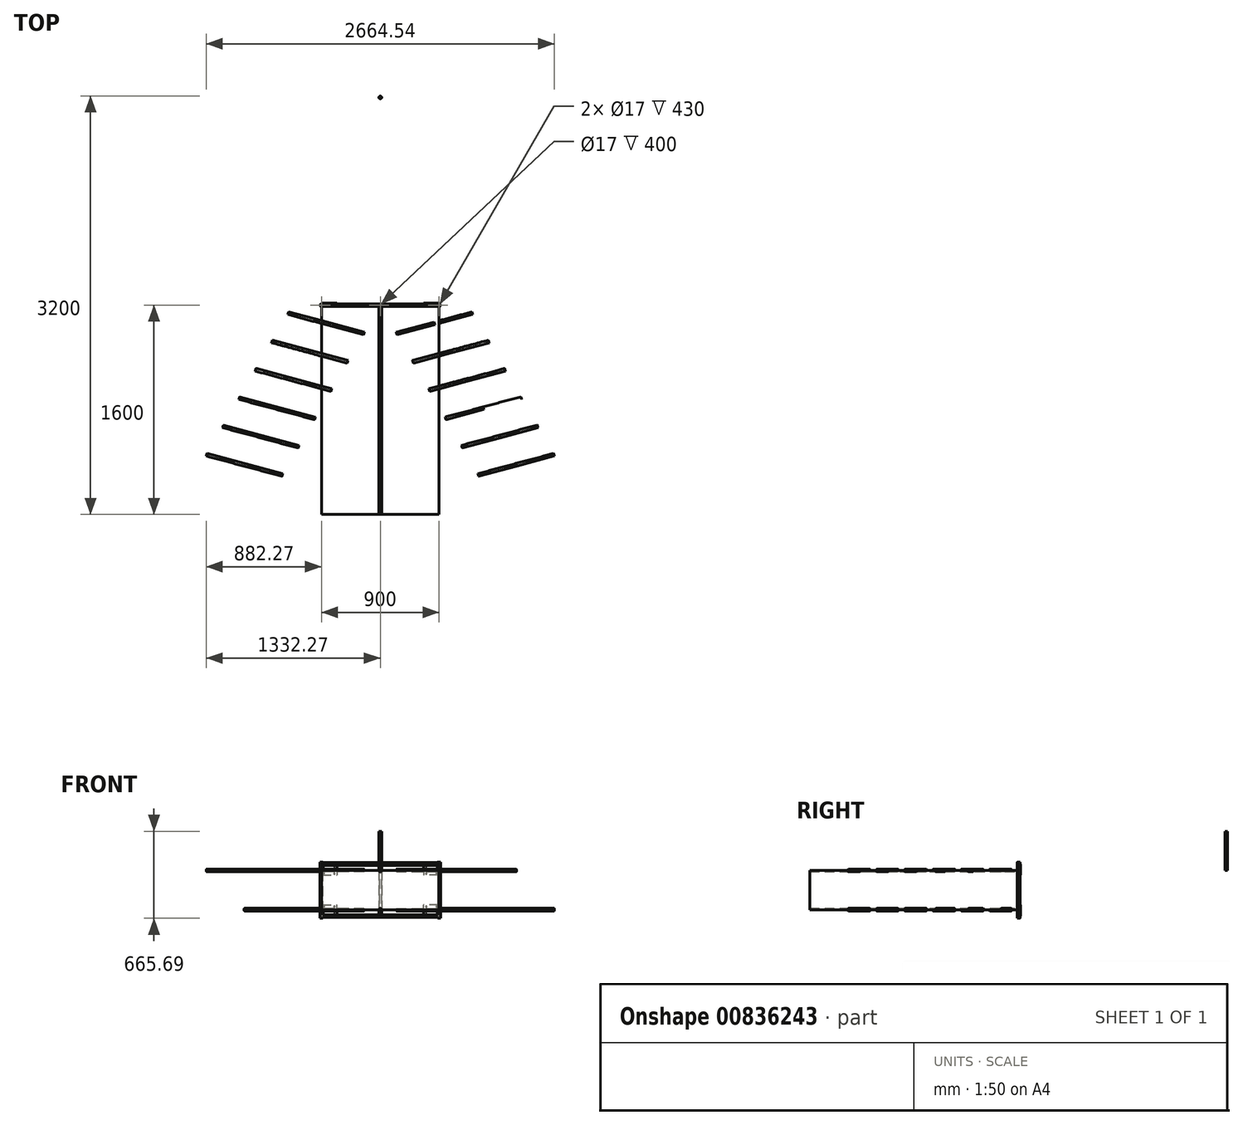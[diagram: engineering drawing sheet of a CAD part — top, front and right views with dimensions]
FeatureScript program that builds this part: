
annotation { "Feature Type Name" : "Feature", "Feature Type Description" : "" }
export const myFeature = defineFeature(function(context is Context, id is Id, definition is map)
    precondition{}
    {
        {
            var Q0;
            Q0=qCreatedBy(makeId("Front.planeOp"),FACE);
            var sketch = newSketch(context, id + "F0", { "sketchPlane" : qUnion([Q0])});
            skLineSegment(sketch, "E0.bottom", {"start": v(450, -150) * mm, "end": v(10.5, -150) * mm});
            skLineSegment(sketch, "E0.left", {"start": v(450, -150) * mm, "end": v(450, 150) * mm});
            skLineSegment(sketch, "E0.right", {"start": v(-450, -150) * mm, "end": v(-450, 150) * mm});
            skPoint(sketch, "E0.middle", {"position": v(0, 0) * mm});
            skLineSegment(sketch, "E1.trimOffspring", {"start": v(-15, 150) * mm, "end": v(-450, 150) * mm});
            skLineSegment(sketch, "E2.trimOffspring", {"start": v(-15, -150) * mm, "end": v(-450, -150) * mm});
            skLineSegment(sketch, "E3", {"start": v(450, -150) * mm, "end": v(-450, -150) * mm});
            skLineSegment(sketch, "E4", {"start": v(-450, 150) * mm, "end": v(450, 150) * mm});
            skCircle(sketch, "E5", {"center": v(0, 150) * mm, "radius": 10.5 * mm});
            skCircle(sketch, "E6", {"center": v(0, -150) * mm, "radius": 10.5 * mm});
            skSolve(sketch);
        }
        {
            var Q0;
            Q0=sQuery(id+"F0.wireOp",EDGE,"E4");
            cPoint(context, id + "F1", {"entities" : qUnion([Q0]), "parameter" : 0.5});
        }
        {
            var Q0;
            Q0=sQuery(id+"F0.wireOp",EDGE,"E4");
            var Q1;
            Q1 = qCreatedBy(id + "F1" ,VERTEX);
            cPlane(context, id + "F2", {"entities" : qUnion([Q0, Q1]), "cplaneType" : CPlaneType.LINE_POINT, "offset" : 25 * mm, "width" : 150 * mm, "height" : 150 * mm});
        }
        {
            var Q0;
            Q0=sQuery(id+"F0.wireOp",EDGE,"E3");
            cPoint(context, id + "F3", {"entities" : qUnion([Q0]), "parameter" : 0.5});
        }
        {
            var Q0;
            Q0 = qCreatedBy(id + "F3" ,VERTEX);
            var Q1;
            Q1=sQuery(id+"F0.wireOp",EDGE,"E3");
            cPlane(context, id + "F4", {"entities" : qUnion([Q0, Q1]), "cplaneType" : CPlaneType.LINE_POINT, "offset" : 25 * mm, "width" : 150 * mm, "height" : 150 * mm});
        }
        {
            var Q0;
            Q0=sQuery(id+"F0.wireOp",EDGE,"E0.left");
            cPoint(context, id + "F5", {"entities" : qUnion([Q0]), "parameter" : 0.5});
        }
        {
            var Q0;
            Q0=sQuery(id+"F0.wireOp",EDGE,"E0.left");
            var Q1;
            Q1 = qCreatedBy(id + "F5" ,VERTEX);
            cPlane(context, id + "F6", {"entities" : qUnion([Q0, Q1]), "cplaneType" : CPlaneType.LINE_POINT, "offset" : 25 * mm, "width" : 150 * mm, "height" : 150 * mm});
        }
        {
            var Q0;
            {var subQ0=sQuery(id+"F0.wireOp",EDGE,"E6");var subQ1=sQuery(id+"F0.wireOp",EDGE,"E3");var subQ2=makeQuery(id+"F0.imprint","INTERSECT",VERTEX,{"disambiguationData":[OD(0.0)],"derivedFrom":[subQ1,subQ0]});Q0=makeQuery(id+"F0.imprint","IMPRINT",FACE,{"disambiguationData":[TD([[makeQuery(id+"F0.imprint","IMPRINT",EDGE,{"disambiguationData":[TD([[subQ2,-1.0]])],"derivedFrom":subQ1}),1.0]])]});}
            var Q1;
            {var subQ0=sQuery(id+"F0.wireOp",EDGE,"E5");var subQ1=sQuery(id+"F0.wireOp",EDGE,"E4");var subQ2=makeQuery(id+"F0.imprint","INTERSECT",VERTEX,{"disambiguationData":[OD(0.0)],"derivedFrom":[subQ1,subQ0]});Q1=makeQuery(id+"F0.imprint","IMPRINT",FACE,{"disambiguationData":[TD([[makeQuery(id+"F0.imprint","IMPRINT",EDGE,{"disambiguationData":[TD([[subQ2,-1.0]])],"derivedFrom":subQ1}),1.0]])]});}
            var Q2;
            {var subQ0=sQuery(id+"F0.wireOp",EDGE,"E6");var subQ1=sQuery(id+"F0.wireOp",EDGE,"E3");var subQ2=makeQuery(id+"F0.imprint","INTERSECT",VERTEX,{"disambiguationData":[OD(0.0)],"derivedFrom":[subQ1,subQ0]});Q2=makeQuery(id+"F0.imprint","IMPRINT",FACE,{"disambiguationData":[TD([[makeQuery(id+"F0.imprint","IMPRINT",EDGE,{"disambiguationData":[TD([[subQ2,-1.0]])],"derivedFrom":subQ1}),-1.0]])]});}
            var Q3;
            {var subQ0=sQuery(id+"F0.wireOp",EDGE,"E5");var subQ1=sQuery(id+"F0.wireOp",EDGE,"E4");var subQ2=makeQuery(id+"F0.imprint","INTERSECT",VERTEX,{"disambiguationData":[OD(0.0)],"derivedFrom":[subQ1,subQ0]});Q3=makeQuery(id+"F0.imprint","IMPRINT",FACE,{"disambiguationData":[TD([[makeQuery(id+"F0.imprint","IMPRINT",EDGE,{"disambiguationData":[TD([[subQ2,-1.0]])],"derivedFrom":subQ1}),-1.0]])]});}
            extrude(context, id + "F7", {"entities" : qUnion([Q0, Q1, Q2, Q3]), "depth" : 1600 * mm, "offsetDistance" : 25 * mm});
        }
        {
            var Q0;
            Q0=qCreatedBy(id+"F4.planeOp",FACE);
            var sketch = newSketch(context, id + "F8", { "sketchPlane" : qUnion([Q0])});
            skCircle(sketch, "E7", {"center": v(0, -198.47) * mm, "radius": 10.5 * mm});
            skSolve(sketch);
        }
        {
            var Q0;
            Q0 = qSketchRegion(id + "F8", true);
            extrude(context, id + "F9", {"entities" : qUnion([Q0]), "operationType" : NewBodyOperationType.ADD, "depth" : 450 * mm, "offsetDistance" : 25 * mm, "hasSecondDirection" : true, "secondDirectionOppositeDirection" : true, "secondDirectionDepth" : 450 * mm});
        }
        {
            var Q0;
            Q0=qCreatedBy(id+"F2.planeOp",FACE);
            var sketch = newSketch(context, id + "F10", { "sketchPlane" : qUnion([Q0])});
            skCircle(sketch, "E8", {"center": v(0, 199.3) * mm, "radius": 10.5 * mm});
            skSolve(sketch);
        }
        {
            var Q0;
            Q0 = qSketchRegion(id + "F10", true);
            extrude(context, id + "F11", {"entities" : qUnion([Q0]), "operationType" : NewBodyOperationType.ADD, "depth" : 450 * mm, "offsetDistance" : 25 * mm, "hasSecondDirection" : true, "secondDirectionOppositeDirection" : true, "secondDirectionDepth" : 450 * mm});
        }
        {
            var Q0;
            Q0=qCreatedBy(id+"F6.planeOp",FACE);
            var sketch = newSketch(context, id + "F12", { "sketchPlane" : qUnion([Q0])});
            skCircle(sketch, "E9", {"center": v(450, 0) * mm, "radius": 10.5 * mm});
            skSolve(sketch);
        }
        {
            var Q0;
            Q0=makeQuery(id+"F11.opExtrude","CAP_FACE",FACE,{"disambiguationData":[OSD([sQuery(id+"F10.wireOp",EDGE,"E8")])],"isStart":true});
            var sketch = newSketch(context, id + "F13", { "sketchPlane" : qUnion([Q0])});
            skLineSegment(sketch, "E10", {"start": v(0, 199.3) * mm, "end": v(0, -200.7) * mm});
            skSolve(sketch);
        }
        {
            var Q0;
            Q0=sQuery(id+"F13.wireOp",EDGE,"E10");
            cPoint(context, id + "F14", {"entities" : qUnion([Q0]), "parameter" : 0.5});
        }
        {
            var Q0;
            Q0=sQuery(id+"F13.wireOp",EDGE,"E10");
            var Q1;
            Q1 = qCreatedBy(id + "F14" ,VERTEX);
            cPlane(context, id + "F15", {"entities" : qUnion([Q0, Q1]), "cplaneType" : CPlaneType.LINE_POINT, "offset" : 25 * mm, "width" : 150 * mm, "height" : 150 * mm});
        }
        {
            var Q0;
            Q0=qCreatedBy(id+"F15.planeOp",FACE);
            var sketch = newSketch(context, id + "F16", { "sketchPlane" : qUnion([Q0])});
            skCircle(sketch, "E11", {"center": v(-450, 0) * mm, "radius": 10.5 * mm});
            skSolve(sketch);
        }
        {
            var Q0;
            Q0=makeQuery(id+"F13.imprint","IMPRINT",FACE,{"disambiguationData":[TD([[makeQuery(id+"F13.imprint","IMPRINT",EDGE,{"derivedFrom":makeQuery(id+"F11.opExtrude","CAP_EDGE",EDGE,{"disambiguationData":[OSD([sQuery(id+"F10.wireOp",EDGE,"E8")])],"isStart":true})}),-1.0]])]});
            var sketch = newSketch(context, id + "F17", { "sketchPlane" : qUnion([Q0])});
            skCircle(sketch, "E12", {"center": v(0, 199.3) * mm, "radius": 8.5 * mm});
            skSolve(sketch);
        }
        {
            var Q0;
            Q0 = qSketchRegion(id + "F17", true);
            extrude(context, id + "F18", {"entities" : qUnion([Q0]), "operationType" : NewBodyOperationType.REMOVE, "oppositeDirection" : true, "depth" : 900 * mm, "offsetDistance" : 25 * mm});
        }
        {
            var Q0;
            Q0=makeQuery(id+"F9.opExtrude","CAP_FACE",FACE,{"disambiguationData":[OSD([sQuery(id+"F8.wireOp",EDGE,"E7")])],"isStart":false});
            var sketch = newSketch(context, id + "F19", { "sketchPlane" : qUnion([Q0])});
            skCircle(sketch, "E13", {"center": v(0, -198.47) * mm, "radius": 8.5 * mm});
            skSolve(sketch);
        }
        {
            var Q0;
            Q0 = qSketchRegion(id + "F19", true);
            extrude(context, id + "F20", {"entities" : qUnion([Q0]), "operationType" : NewBodyOperationType.REMOVE, "oppositeDirection" : true, "depth" : 900 * mm, "offsetDistance" : 25 * mm});
        }
        {
            var Q0;
            Q0 = qSketchRegion(id + "F12", true);
            extrude(context, id + "F21", {"entities" : qUnion([Q0]), "depth" : 215 * mm, "offsetDistance" : 25 * mm, "hasSecondDirection" : true, "secondDirectionOppositeDirection" : true, "secondDirectionDepth" : 215 * mm});
        }
        {
            var Q0;
            Q0=makeQuery(id+"F21.opExtrude","CAP_FACE",FACE,{"disambiguationData":[OSD([sQuery(id+"F12.wireOp",EDGE,"E9")])],"isStart":false});
            var sketch = newSketch(context, id + "F22", { "sketchPlane" : qUnion([Q0])});
            skCircle(sketch, "E14", {"center": v(450, 0) * mm, "radius": 8.5 * mm});
            skSolve(sketch);
        }
        {
            var Q0;
            Q0 = qSketchRegion(id + "F22", true);
            extrude(context, id + "F23", {"entities" : qUnion([Q0]), "operationType" : NewBodyOperationType.REMOVE, "oppositeDirection" : true, "depth" : 460 * mm, "offsetDistance" : 25 * mm});
        }
        {
            var Q0;
            Q0 = qSketchRegion(id + "F16", true);
            extrude(context, id + "F24", {"entities" : qUnion([Q0]), "depth" : 215 * mm, "offsetDistance" : 25 * mm, "hasSecondDirection" : true, "secondDirectionOppositeDirection" : true, "secondDirectionDepth" : 215 * mm});
        }
        {
            var Q0;
            Q0=makeQuery(id+"F24.opExtrude","CAP_FACE",FACE,{"disambiguationData":[OSD([sQuery(id+"F16.wireOp",EDGE,"E11")])],"isStart":true});
            var sketch = newSketch(context, id + "F25", { "sketchPlane" : qUnion([Q0])});
            skCircle(sketch, "E15", {"center": v(-450, 0) * mm, "radius": 8.5 * mm});
            skSolve(sketch);
        }
        {
            var Q0;
            Q0 = qSketchRegion(id + "F25", true);
            extrude(context, id + "F26", {"entities" : qUnion([Q0]), "operationType" : NewBodyOperationType.REMOVE, "oppositeDirection" : true, "depth" : 460 * mm, "offsetDistance" : 25 * mm});
        }
        {
            var Q0;
            Q0=makeQuery(id+"F7.opExtrude","CAP_FACE",FACE,{"disambiguationData":[OSD([sQuery(id+"F0.wireOp",EDGE,"E5")])],"isStart":false});
            var sketch = newSketch(context, id + "F27", { "sketchPlane" : qUnion([Q0])});
            skCircle(sketch, "E16", {"center": v(0, 150) * mm, "radius": 8.5 * mm});
            skSolve(sketch);
        }
        {
            var Q0;
            Q0 = qSketchRegion(id + "F27", true);
            extrude(context, id + "F28", {"entities" : qUnion([Q0]), "operationType" : NewBodyOperationType.REMOVE, "oppositeDirection" : true, "depth" : 1600 * mm, "offsetDistance" : 25 * mm});
        }
        {
            var Q0;
            Q0=makeQuery(id+"F7.opExtrude","SWEPT_FACE",FACE,{"disambiguationData":[OSD([sQuery(id+"F0.wireOp",EDGE,"E6")])]});
            var Q1;
            Q1=makeQuery(id+"F9.opExtrude","SWEPT_FACE",FACE,{"disambiguationData":[OSD([sQuery(id+"F8.wireOp",EDGE,"E7")])]});
            cPlane(context, id + "F29", {"entities" : qUnion([Q0, Q1]), "cplaneType" : CPlaneType.LINE_ANGLE, "offset" : 25 * mm, "angle" : 0 * degree, "width" : 150 * mm, "height" : 150 * mm});
        }
        {
            var Q0;
            Q0=qCreatedBy(id+"F29.planeOp",FACE);
            var sketch = newSketch(context, id + "F30", { "sketchPlane" : qUnion([Q0])});
            skLineSegment(sketch, "E17", {"start": v(0, 0) * mm, "end": v(0, 1600) * mm});
            skLineSegment(sketch, "E18", {"start": v(0, 250) * mm, "end": v(579.56, 405.3) * mm});
            skLineSegment(sketch, "E19", {"start": v(0, 250) * mm, "end": v(-289.78, 327.65) * mm});
            skLineSegment(sketch, "E20", {"start": v(0, 500) * mm, "end": v(579.56, 655.3) * mm});
            skLineSegment(sketch, "E21", {"start": v(0, 500) * mm, "end": v(-289.78, 577.65) * mm});
            skLineSegment(sketch, "E22", {"start": v(0, 750) * mm, "end": v(579.56, 905.3) * mm});
            skLineSegment(sketch, "E23", {"start": v(0, 750) * mm, "end": v(-289.78, 827.65) * mm});
            skLineSegment(sketch, "E24", {"start": v(0, 1000) * mm, "end": v(579.56, 1155.3) * mm});
            skLineSegment(sketch, "E25", {"start": v(0, 1000) * mm, "end": v(-289.78, 1077.65) * mm});
            skLineSegment(sketch, "E26", {"start": v(0, 1250) * mm, "end": v(579.56, 1405.3) * mm});
            skLineSegment(sketch, "E27", {"start": v(0, 1250) * mm, "end": v(-289.78, 1327.65) * mm});
            skLineSegment(sketch, "E28", {"start": v(0, 1500) * mm, "end": v(579.56, 1655.3) * mm});
            skLineSegment(sketch, "E29", {"start": v(0, 1500) * mm, "end": v(-289.78, 1577.65) * mm});
            skSolve(sketch);
        }
        {
            var Q0;
            Q0=makeQuery(id+"F7.opExtrude","SWEPT_FACE",FACE,{"disambiguationData":[OSD([sQuery(id+"F0.wireOp",EDGE,"E5")])]});
            var Q1;
            Q1=makeQuery(id+"F11.opExtrude","SWEPT_FACE",FACE,{"disambiguationData":[OSD([sQuery(id+"F10.wireOp",EDGE,"E8")])]});
            cPlane(context, id + "F31", {"entities" : qUnion([Q0, Q1]), "cplaneType" : CPlaneType.LINE_ANGLE, "offset" : 25 * mm, "angle" : 0 * degree, "width" : 150 * mm, "height" : 150 * mm});
        }
        {
            var Q0;
            Q0=qCreatedBy(id+"F31.planeOp",FACE);
            var sketch = newSketch(context, id + "F32", { "sketchPlane" : qUnion([Q0])});
            skLineSegment(sketch, "E30", {"start": v(0, 0) * mm, "end": v(0, -1600) * mm});
            skLineSegment(sketch, "E31", {"start": v(0, -250) * mm, "end": v(-579.56, -405.3) * mm});
            skLineSegment(sketch, "E32", {"start": v(0, -500) * mm, "end": v(-579.56, -655.3) * mm});
            skLineSegment(sketch, "E33", {"start": v(0, -750) * mm, "end": v(-579.56, -905.3) * mm});
            skLineSegment(sketch, "E34", {"start": v(0, -1000) * mm, "end": v(-579.56, -1155.3) * mm});
            skLineSegment(sketch, "E35", {"start": v(0, -1250) * mm, "end": v(-579.56, -1405.3) * mm});
            skLineSegment(sketch, "E36", {"start": v(0, -1500) * mm, "end": v(-579.56, -1655.3) * mm});
            skLineSegment(sketch, "E37", {"start": v(0, -250) * mm, "end": v(289.78, -327.65) * mm});
            skLineSegment(sketch, "E38", {"start": v(0, -500) * mm, "end": v(289.78, -577.65) * mm});
            skLineSegment(sketch, "E39", {"start": v(0, -750) * mm, "end": v(289.78, -827.65) * mm});
            skLineSegment(sketch, "E40", {"start": v(0, -1000) * mm, "end": v(289.78, -1077.65) * mm});
            skLineSegment(sketch, "E41", {"start": v(0, -1250) * mm, "end": v(289.78, -1327.65) * mm});
            skLineSegment(sketch, "E42", {"start": v(0, -1500) * mm, "end": v(289.78, -1577.65) * mm});
            skSolve(sketch);
        }
        {
            var Q0;
            Q0=sQuery(id+"F32.wireOp",VERTEX,"E36.start");
            var Q1;
            Q1=sQuery(id+"F32.wireOp",VERTEX,"E36.end");
            cPlane(context, id + "F33", {"entities" : qUnion([Q0, Q1]), "cplaneType" : CPlaneType.MID_PLANE, "offset" : 25 * mm, "oppositeDirection" : true, "width" : 150 * mm, "height" : 150 * mm});
        }
        {
            var Q0;
            Q0=qCreatedBy(id+"F33.planeOp",FACE);
            var sketch = newSketch(context, id + "F34", { "sketchPlane" : qUnion([Q0])});
            skCircle(sketch, "E43", {"center": v(1448.89, 150) * mm, "radius": 10.5 * mm});
            skSolve(sketch);
        }
        {
            var Q0;
            Q0 = qSketchRegion(id + "F34", true);
            extrude(context, id + "F35", {"entities" : qUnion([Q0]), "operationType" : NewBodyOperationType.ADD, "oppositeDirection" : true, "depth" : 300 * mm, "offsetDistance" : 25 * mm, "hasSecondDirection" : true, "secondDirectionOppositeDirection" : false, "secondDirectionDepth" : 300 * mm});
        }
        {
            var Q0;
            Q0=sQuery(id+"F32.wireOp",EDGE,"E35");
            cPlane(context, id + "F36", {"entities" : qUnion([Q0]), "cplaneType" : CPlaneType.MID_PLANE, "offset" : 25 * mm, "width" : 150 * mm, "height" : 150 * mm});
        }
        {
            var Q0;
            Q0=qCreatedBy(id+"F36.planeOp",FACE);
            var sketch = newSketch(context, id + "F37", { "sketchPlane" : qUnion([Q0])});
            skCircle(sketch, "E44", {"center": v(1207.4, 150) * mm, "radius": 10.5 * mm});
            skSolve(sketch);
        }
        {
            var Q0;
            Q0 = qSketchRegion(id + "F37", true);
            extrude(context, id + "F38", {"entities" : qUnion([Q0]), "operationType" : NewBodyOperationType.ADD, "depth" : 300 * mm, "offsetDistance" : 25 * mm, "hasSecondDirection" : true, "secondDirectionOppositeDirection" : true, "secondDirectionDepth" : 300 * mm});
        }
        {
            var Q0;
            Q0=sQuery(id+"F32.wireOp",EDGE,"E34");
            cPlane(context, id + "F39", {"entities" : qUnion([Q0]), "cplaneType" : CPlaneType.MID_PLANE, "offset" : 25 * mm, "width" : 150 * mm, "height" : 150 * mm});
        }
        {
            var Q0;
            Q0=qCreatedBy(id+"F39.planeOp",FACE);
            var sketch = newSketch(context, id + "F40", { "sketchPlane" : qUnion([Q0])});
            skCircle(sketch, "E45", {"center": v(965.93, 150) * mm, "radius": 10.5 * mm});
            skSolve(sketch);
        }
        {
            var Q0;
            Q0 = qSketchRegion(id + "F40", true);
            extrude(context, id + "F41", {"entities" : qUnion([Q0]), "operationType" : NewBodyOperationType.ADD, "depth" : 300 * mm, "offsetDistance" : 25 * mm, "hasSecondDirection" : true, "secondDirectionOppositeDirection" : true, "secondDirectionDepth" : 300 * mm});
        }
        {
            var Q0;
            Q0=sQuery(id+"F32.wireOp",EDGE,"E33");
            cPlane(context, id + "F42", {"entities" : qUnion([Q0]), "cplaneType" : CPlaneType.MID_PLANE, "offset" : 25 * mm, "width" : 150 * mm, "height" : 150 * mm});
        }
        {
            var Q0;
            Q0=qCreatedBy(id+"F42.planeOp",FACE);
            var sketch = newSketch(context, id + "F43", { "sketchPlane" : qUnion([Q0])});
            skCircle(sketch, "E46", {"center": v(724.44, 150) * mm, "radius": 10.5 * mm});
            skSolve(sketch);
        }
        {
            var Q0;
            Q0 = qSketchRegion(id + "F43", true);
            extrude(context, id + "F44", {"entities" : qUnion([Q0]), "operationType" : NewBodyOperationType.ADD, "depth" : 300 * mm, "offsetDistance" : 25 * mm, "hasSecondDirection" : true, "secondDirectionOppositeDirection" : true, "secondDirectionDepth" : 300 * mm});
        }
        {
            var Q0;
            Q0=sQuery(id+"F32.wireOp",EDGE,"E32");
            cPlane(context, id + "F45", {"entities" : qUnion([Q0]), "cplaneType" : CPlaneType.MID_PLANE, "offset" : 25 * mm, "width" : 150 * mm, "height" : 150 * mm});
        }
        {
            var Q0;
            Q0=qCreatedBy(id+"F45.planeOp",FACE);
            var sketch = newSketch(context, id + "F46", { "sketchPlane" : qUnion([Q0])});
            skCircle(sketch, "E47", {"center": v(482.96, 150) * mm, "radius": 10.5 * mm});
            skSolve(sketch);
        }
        {
            var Q0;
            Q0 = qSketchRegion(id + "F46", true);
            extrude(context, id + "F47", {"entities" : qUnion([Q0]), "operationType" : NewBodyOperationType.ADD, "depth" : 300 * mm, "offsetDistance" : 25 * mm, "hasSecondDirection" : true, "secondDirectionOppositeDirection" : true, "secondDirectionDepth" : 300 * mm});
        }
        {
            var Q0;
            Q0=sQuery(id+"F32.wireOp",EDGE,"E31");
            cPlane(context, id + "F48", {"entities" : qUnion([Q0]), "cplaneType" : CPlaneType.MID_PLANE, "offset" : 25 * mm, "width" : 150 * mm, "height" : 150 * mm});
        }
        {
            var Q0;
            Q0=qCreatedBy(id+"F48.planeOp",FACE);
            var sketch = newSketch(context, id + "F49", { "sketchPlane" : qUnion([Q0])});
            skCircle(sketch, "E48", {"center": v(241.48, 150) * mm, "radius": 10.5 * mm});
            skSolve(sketch);
        }
        {
            var Q0;
            Q0 = qSketchRegion(id + "F49", true);
            extrude(context, id + "F50", {"entities" : qUnion([Q0]), "operationType" : NewBodyOperationType.ADD, "depth" : 300 * mm, "offsetDistance" : 25 * mm, "hasSecondDirection" : true, "secondDirectionOppositeDirection" : true, "secondDirectionDepth" : 300 * mm});
        }
        {
            var Q0;
            Q0=sQuery(id+"F30.wireOp",EDGE,"E29");
            cPlane(context, id + "F51", {"entities" : qUnion([Q0]), "cplaneType" : CPlaneType.MID_PLANE, "offset" : 25 * mm, "width" : 150 * mm, "height" : 150 * mm});
        }
        {
            var Q0;
            Q0=qCreatedBy(id+"F51.planeOp",FACE);
            var sketch = newSketch(context, id + "F52", { "sketchPlane" : qUnion([Q0])});
            skCircle(sketch, "E49", {"center": v(1448.89, -150) * mm, "radius": 10.5 * mm});
            skSolve(sketch);
        }
        {
            var Q0;
            Q0 = qSketchRegion(id + "F52", true);
            extrude(context, id + "F53", {"entities" : qUnion([Q0]), "operationType" : NewBodyOperationType.ADD, "depth" : 150 * mm, "offsetDistance" : 25 * mm, "hasSecondDirection" : true, "secondDirectionOppositeDirection" : true, "secondDirectionDepth" : 150 * mm});
        }
        {
            var Q0;
            Q0=sQuery(id+"F30.wireOp",EDGE,"E27");
            cPlane(context, id + "F54", {"entities" : qUnion([Q0]), "cplaneType" : CPlaneType.MID_PLANE, "offset" : 25 * mm, "width" : 150 * mm, "height" : 150 * mm});
        }
        {
            var Q0;
            Q0=qCreatedBy(id+"F54.planeOp",FACE);
            var sketch = newSketch(context, id + "F55", { "sketchPlane" : qUnion([Q0])});
            skCircle(sketch, "E50", {"center": v(1207.4, -150) * mm, "radius": 10.5 * mm});
            skSolve(sketch);
        }
        {
            var Q0;
            Q0 = qSketchRegion(id + "F55", true);
            extrude(context, id + "F56", {"entities" : qUnion([Q0]), "operationType" : NewBodyOperationType.ADD, "depth" : 150 * mm, "offsetDistance" : 25 * mm, "hasSecondDirection" : true, "secondDirectionOppositeDirection" : true, "secondDirectionDepth" : 150 * mm});
        }
        {
            var Q0;
            Q0=sQuery(id+"F30.wireOp",EDGE,"E25");
            cPlane(context, id + "F57", {"entities" : qUnion([Q0]), "cplaneType" : CPlaneType.MID_PLANE, "offset" : 25 * mm, "width" : 150 * mm, "height" : 150 * mm});
        }
        {
            var Q0;
            Q0=qCreatedBy(id+"F57.planeOp",FACE);
            var sketch = newSketch(context, id + "F58", { "sketchPlane" : qUnion([Q0])});
            skCircle(sketch, "E51", {"center": v(965.93, -150) * mm, "radius": 10.5 * mm});
            skSolve(sketch);
        }
        {
            var Q0;
            Q0 = qSketchRegion(id + "F58", true);
            extrude(context, id + "F59", {"entities" : qUnion([Q0]), "operationType" : NewBodyOperationType.ADD, "depth" : 150 * mm, "offsetDistance" : 25 * mm, "hasSecondDirection" : true, "secondDirectionOppositeDirection" : true, "secondDirectionDepth" : 150 * mm});
        }
        {
            var Q0;
            Q0=sQuery(id+"F30.wireOp",EDGE,"E23");
            cPlane(context, id + "F60", {"entities" : qUnion([Q0]), "cplaneType" : CPlaneType.MID_PLANE, "offset" : 25 * mm, "width" : 150 * mm, "height" : 150 * mm});
        }
        {
            var Q0;
            Q0=qCreatedBy(id+"F60.planeOp",FACE);
            var sketch = newSketch(context, id + "F61", { "sketchPlane" : qUnion([Q0])});
            skCircle(sketch, "E52", {"center": v(724.44, -150) * mm, "radius": 10.5 * mm});
            skSolve(sketch);
        }
        {
            var Q0;
            Q0 = qSketchRegion(id + "F61", true);
            extrude(context, id + "F62", {"entities" : qUnion([Q0]), "operationType" : NewBodyOperationType.ADD, "depth" : 150 * mm, "offsetDistance" : 25 * mm, "hasSecondDirection" : true, "secondDirectionOppositeDirection" : true, "secondDirectionDepth" : 150 * mm});
        }
        {
            var Q0;
            Q0=sQuery(id+"F30.wireOp",EDGE,"E21");
            cPlane(context, id + "F63", {"entities" : qUnion([Q0]), "cplaneType" : CPlaneType.MID_PLANE, "offset" : 25 * mm, "width" : 150 * mm, "height" : 150 * mm});
        }
        {
            var Q0;
            Q0=qCreatedBy(id+"F63.planeOp",FACE);
            var sketch = newSketch(context, id + "F64", { "sketchPlane" : qUnion([Q0])});
            skCircle(sketch, "E53", {"center": v(482.96, -150) * mm, "radius": 10.5 * mm});
            skSolve(sketch);
        }
        {
            var Q0;
            Q0 = qSketchRegion(id + "F64", true);
            extrude(context, id + "F65", {"entities" : qUnion([Q0]), "operationType" : NewBodyOperationType.ADD, "depth" : 150 * mm, "offsetDistance" : 25 * mm, "hasSecondDirection" : true, "secondDirectionOppositeDirection" : true, "secondDirectionDepth" : 150 * mm});
        }
        {
            var Q0;
            Q0=sQuery(id+"F30.wireOp",EDGE,"E19");
            cPlane(context, id + "F66", {"entities" : qUnion([Q0]), "cplaneType" : CPlaneType.MID_PLANE, "offset" : 25 * mm, "width" : 150 * mm, "height" : 150 * mm});
        }
        {
            var Q0;
            Q0=qCreatedBy(id+"F66.planeOp",FACE);
            var sketch = newSketch(context, id + "F67", { "sketchPlane" : qUnion([Q0])});
            skCircle(sketch, "E54", {"center": v(241.48, -150) * mm, "radius": 10.5 * mm});
            skSolve(sketch);
        }
        {
            var Q0;
            Q0 = qSketchRegion(id + "F67", true);
            extrude(context, id + "F68", {"entities" : qUnion([Q0]), "operationType" : NewBodyOperationType.ADD, "depth" : 150 * mm, "offsetDistance" : 25 * mm, "hasSecondDirection" : true, "secondDirectionOppositeDirection" : true, "secondDirectionDepth" : 150 * mm});
        }
        {
            var Q0;
            Q0=sQuery(id+"F30.wireOp",EDGE,"E28");
            cPlane(context, id + "F69", {"entities" : qUnion([Q0]), "cplaneType" : CPlaneType.MID_PLANE, "offset" : 25 * mm, "width" : 150 * mm, "height" : 150 * mm});
        }
        {
            var Q0;
            Q0=qCreatedBy(id+"F69.planeOp",FACE);
            var sketch = newSketch(context, id + "F70", { "sketchPlane" : qUnion([Q0])});
            skCircle(sketch, "E55", {"center": v(-1448.89, -150) * mm, "radius": 10.5 * mm});
            skSolve(sketch);
        }
        {
            var Q0;
            Q0 = qSketchRegion(id + "F70", true);
            extrude(context, id + "F71", {"entities" : qUnion([Q0]), "operationType" : NewBodyOperationType.ADD, "depth" : 300 * mm, "offsetDistance" : 25 * mm, "hasSecondDirection" : true, "secondDirectionOppositeDirection" : true, "secondDirectionDepth" : 300 * mm});
        }
        {
            var Q0;
            Q0=sQuery(id+"F30.wireOp",EDGE,"E26");
            cPlane(context, id + "F72", {"entities" : qUnion([Q0]), "cplaneType" : CPlaneType.MID_PLANE, "offset" : 25 * mm, "width" : 150 * mm, "height" : 150 * mm});
        }
        {
            var Q0;
            Q0=qCreatedBy(id+"F72.planeOp",FACE);
            var sketch = newSketch(context, id + "F73", { "sketchPlane" : qUnion([Q0])});
            skCircle(sketch, "E56", {"center": v(-1207.4, -150) * mm, "radius": 10.5 * mm});
            skSolve(sketch);
        }
        {
            var Q0;
            Q0 = qSketchRegion(id + "F73", true);
            extrude(context, id + "F74", {"entities" : qUnion([Q0]), "operationType" : NewBodyOperationType.ADD, "depth" : 300 * mm, "offsetDistance" : 25 * mm, "hasSecondDirection" : true, "secondDirectionOppositeDirection" : true, "secondDirectionDepth" : 300 * mm});
        }
        {
            var Q0;
            Q0=sQuery(id+"F30.wireOp",EDGE,"E24");
            cPlane(context, id + "F75", {"entities" : qUnion([Q0]), "cplaneType" : CPlaneType.MID_PLANE, "offset" : 25 * mm, "width" : 150 * mm, "height" : 150 * mm});
        }
        {
            var Q0;
            Q0=qCreatedBy(id+"F75.planeOp",FACE);
            var sketch = newSketch(context, id + "F76", { "sketchPlane" : qUnion([Q0])});
            skCircle(sketch, "E57", {"center": v(-965.93, -150) * mm, "radius": 10.5 * mm});
            skSolve(sketch);
        }
        {
            var Q0;
            Q0 = qSketchRegion(id + "F76", true);
            extrude(context, id + "F77", {"entities" : qUnion([Q0]), "operationType" : NewBodyOperationType.ADD, "depth" : 300 * mm, "offsetDistance" : 25 * mm, "hasSecondDirection" : true, "secondDirectionOppositeDirection" : true, "secondDirectionDepth" : 300 * mm});
        }
        {
            var Q0;
            Q0=sQuery(id+"F30.wireOp",EDGE,"E22");
            cPlane(context, id + "F78", {"entities" : qUnion([Q0]), "cplaneType" : CPlaneType.MID_PLANE, "offset" : 25 * mm, "width" : 150 * mm, "height" : 150 * mm});
        }
        {
            var Q0;
            Q0=qCreatedBy(id+"F78.planeOp",FACE);
            var sketch = newSketch(context, id + "F79", { "sketchPlane" : qUnion([Q0])});
            skCircle(sketch, "E58", {"center": v(-724.44, -150) * mm, "radius": 10.5 * mm});
            skSolve(sketch);
        }
        {
            var Q0;
            Q0 = qSketchRegion(id + "F79", true);
            extrude(context, id + "F80", {"entities" : qUnion([Q0]), "operationType" : NewBodyOperationType.ADD, "depth" : 300 * mm, "offsetDistance" : 25 * mm, "hasSecondDirection" : true, "secondDirectionOppositeDirection" : true, "secondDirectionDepth" : 300 * mm});
        }
        {
            var Q0;
            Q0=sQuery(id+"F30.wireOp",EDGE,"E20");
            cPlane(context, id + "F81", {"entities" : qUnion([Q0]), "cplaneType" : CPlaneType.MID_PLANE, "offset" : 25 * mm, "width" : 150 * mm, "height" : 150 * mm});
        }
        {
            var Q0;
            Q0=qCreatedBy(id+"F81.planeOp",FACE);
            var sketch = newSketch(context, id + "F82", { "sketchPlane" : qUnion([Q0])});
            skCircle(sketch, "E59", {"center": v(-482.96, -150) * mm, "radius": 10.5 * mm});
            skSolve(sketch);
        }
        {
            var Q0;
            Q0 = qSketchRegion(id + "F82", true);
            extrude(context, id + "F83", {"entities" : qUnion([Q0]), "operationType" : NewBodyOperationType.ADD, "depth" : 300 * mm, "offsetDistance" : 25 * mm, "hasSecondDirection" : true, "secondDirectionOppositeDirection" : true, "secondDirectionDepth" : 300 * mm});
        }
        {
            var Q0;
            Q0=sQuery(id+"F30.wireOp",EDGE,"E18");
            cPlane(context, id + "F84", {"entities" : qUnion([Q0]), "cplaneType" : CPlaneType.MID_PLANE, "offset" : 25 * mm, "width" : 150 * mm, "height" : 150 * mm});
        }
        {
            var Q0;
            Q0=qCreatedBy(id+"F84.planeOp",FACE);
            var sketch = newSketch(context, id + "F85", { "sketchPlane" : qUnion([Q0])});
            skCircle(sketch, "E60", {"center": v(-241.48, -150) * mm, "radius": 10.5 * mm});
            skSolve(sketch);
        }
        {
            var Q0;
            Q0 = qSketchRegion(id + "F85", true);
            extrude(context, id + "F86", {"entities" : qUnion([Q0]), "operationType" : NewBodyOperationType.ADD, "depth" : 300 * mm, "offsetDistance" : 25 * mm, "hasSecondDirection" : true, "secondDirectionOppositeDirection" : true, "secondDirectionDepth" : 300 * mm});
        }
        {
            var Q0;
            Q0=sQuery(id+"F32.wireOp",EDGE,"E42");
            cPlane(context, id + "F87", {"entities" : qUnion([Q0]), "cplaneType" : CPlaneType.MID_PLANE, "offset" : 25 * mm, "width" : 150 * mm, "height" : 150 * mm});
        }
        {
            var Q0;
            Q0=qCreatedBy(id+"F87.planeOp",FACE);
            var sketch = newSketch(context, id + "F88", { "sketchPlane" : qUnion([Q0])});
            skCircle(sketch, "E61", {"center": v(-1448.89, 150) * mm, "radius": 10.5 * mm});
            skSolve(sketch);
        }
        {
            var Q0;
            Q0 = qSketchRegion(id + "F88", true);
            extrude(context, id + "F89", {"entities" : qUnion([Q0]), "operationType" : NewBodyOperationType.ADD, "depth" : 150 * mm, "offsetDistance" : 25 * mm, "hasSecondDirection" : true, "secondDirectionOppositeDirection" : true, "secondDirectionDepth" : 150 * mm});
        }
        {
            var Q0;
            Q0=sQuery(id+"F32.wireOp",EDGE,"E41");
            cPlane(context, id + "F90", {"entities" : qUnion([Q0]), "cplaneType" : CPlaneType.MID_PLANE, "offset" : 25 * mm, "width" : 150 * mm, "height" : 150 * mm});
        }
        {
            var Q0;
            Q0=qCreatedBy(id+"F90.planeOp",FACE);
            var sketch = newSketch(context, id + "F91", { "sketchPlane" : qUnion([Q0])});
            skCircle(sketch, "E62", {"center": v(-1207.4, 150) * mm, "radius": 10.5 * mm});
            skSolve(sketch);
        }
        {
            var Q0;
            Q0 = qSketchRegion(id + "F91", true);
            extrude(context, id + "F92", {"entities" : qUnion([Q0]), "operationType" : NewBodyOperationType.ADD, "depth" : 150 * mm, "offsetDistance" : 25 * mm, "hasSecondDirection" : true, "secondDirectionOppositeDirection" : true, "secondDirectionDepth" : 150 * mm});
        }
        {
            var Q0;
            Q0=sQuery(id+"F32.wireOp",EDGE,"E40");
            cPlane(context, id + "F93", {"entities" : qUnion([Q0]), "cplaneType" : CPlaneType.MID_PLANE, "offset" : 25 * mm, "width" : 150 * mm, "height" : 150 * mm});
        }
        {
            var Q0;
            Q0=qCreatedBy(id+"F93.planeOp",FACE);
            var sketch = newSketch(context, id + "F94", { "sketchPlane" : qUnion([Q0])});
            skCircle(sketch, "E63", {"center": v(-965.93, 150) * mm, "radius": 10.5 * mm});
            skSolve(sketch);
        }
        {
            var Q0;
            Q0 = qSketchRegion(id + "F94", true);
            extrude(context, id + "F95", {"entities" : qUnion([Q0]), "operationType" : NewBodyOperationType.ADD, "depth" : 150 * mm, "offsetDistance" : 25 * mm, "hasSecondDirection" : true, "secondDirectionOppositeDirection" : true, "secondDirectionDepth" : 150 * mm});
        }
        {
            var Q0;
            Q0=sQuery(id+"F32.wireOp",EDGE,"E39");
            cPlane(context, id + "F96", {"entities" : qUnion([Q0]), "cplaneType" : CPlaneType.MID_PLANE, "offset" : 25 * mm, "width" : 150 * mm, "height" : 150 * mm});
        }
        {
            var Q0;
            Q0=qCreatedBy(id+"F96.planeOp",FACE);
            var sketch = newSketch(context, id + "F97", { "sketchPlane" : qUnion([Q0])});
            skCircle(sketch, "E64", {"center": v(-724.44, 150) * mm, "radius": 10.5 * mm});
            skSolve(sketch);
        }
        {
            var Q0;
            Q0 = qSketchRegion(id + "F97", true);
            extrude(context, id + "F98", {"entities" : qUnion([Q0]), "operationType" : NewBodyOperationType.ADD, "depth" : 150 * mm, "offsetDistance" : 25 * mm, "hasSecondDirection" : true, "secondDirectionOppositeDirection" : true, "secondDirectionDepth" : 150 * mm});
        }
        {
            var Q0;
            Q0=sQuery(id+"F32.wireOp",EDGE,"E38");
            cPlane(context, id + "F99", {"entities" : qUnion([Q0]), "cplaneType" : CPlaneType.MID_PLANE, "offset" : 25 * mm, "width" : 150 * mm, "height" : 150 * mm});
        }
        {
            var Q0;
            Q0=qCreatedBy(id+"F99.planeOp",FACE);
            var sketch = newSketch(context, id + "F100", { "sketchPlane" : qUnion([Q0])});
            skCircle(sketch, "E65", {"center": v(-482.96, 150) * mm, "radius": 10.5 * mm});
            skSolve(sketch);
        }
        {
            var Q0;
            Q0 = qSketchRegion(id + "F100", true);
            extrude(context, id + "F101", {"entities" : qUnion([Q0]), "operationType" : NewBodyOperationType.ADD, "depth" : 150 * mm, "offsetDistance" : 25 * mm, "hasSecondDirection" : true, "secondDirectionOppositeDirection" : true, "secondDirectionDepth" : 150 * mm});
        }
        {
            var Q0;
            Q0=sQuery(id+"F32.wireOp",EDGE,"E37");
            cPlane(context, id + "F102", {"entities" : qUnion([Q0]), "cplaneType" : CPlaneType.MID_PLANE, "offset" : 25 * mm, "width" : 150 * mm, "height" : 150 * mm});
        }
        {
            var Q0;
            Q0=qCreatedBy(id+"F102.planeOp",FACE);
            var sketch = newSketch(context, id + "F103", { "sketchPlane" : qUnion([Q0])});
            skCircle(sketch, "E66", {"center": v(-241.48, 150) * mm, "radius": 10.5 * mm});
            skSolve(sketch);
        }
        {
            var Q0;
            Q0 = qSketchRegion(id + "F103", true);
            extrude(context, id + "F104", {"entities" : qUnion([Q0]), "operationType" : NewBodyOperationType.ADD, "depth" : 150 * mm, "offsetDistance" : 25 * mm, "hasSecondDirection" : true, "secondDirectionOppositeDirection" : true, "secondDirectionDepth" : 150 * mm});
        }
        {
            var Q0;
            Q0=sQuery(id+"F32.wireOp",EDGE,"E30");
            var Q1;
            Q1=sQuery(id+"F32.wireOp",EDGE,"E42");
            cPlane(context, id + "F105", {"entities" : qUnion([Q0, Q1]), "cplaneType" : CPlaneType.LINE_ANGLE, "offset" : 25 * mm, "angle" : 0 * degree, "width" : 150 * mm, "height" : 150 * mm});
        }
        {
            var Q0;
            Q0=qCreatedBy(id+"F105.planeOp",FACE);
            var sketch = newSketch(context, id + "F106", { "sketchPlane" : qUnion([Q0])});
            skCircle(sketch, "E67", {"center": v(0, -1589.5) * mm, "radius": 10.5 * mm});
            skLineSegment(sketch, "E68", {"start": v(0, -1600) * mm, "end": v(0, -1589.5) * mm});
            skSolve(sketch);
        }
        {
            var Q0;
            Q0 = qSketchRegion(id + "F106", true);
            extrude(context, id + "F107", {"entities" : qUnion([Q0]), "operationType" : NewBodyOperationType.ADD, "oppositeDirection" : true, "depth" : 300 * mm, "offsetDistance" : 25 * mm});
        }
        {
            var Q0;
            Q0=qCreatedBy(id+"F6.planeOp",FACE);
            var sketch = newSketch(context, id + "F108", { "sketchPlane" : qUnion([Q0])});
            skCircle(sketch, "E69", {"center": v(0, 0) * mm, "radius": 10.5 * mm});
            skCircle(sketch, "E70", {"center": v(0, 0) * mm, "radius": 8.5 * mm});
            skSolve(sketch);
        }
        {
            var Q0;
            Q0=makeQuery(id+"F108.imprint","IMPRINT",FACE,{"disambiguationData":[TD([[makeQuery(id+"F108.imprint","IMPRINT",EDGE,{"derivedFrom":sQuery(id+"F108.wireOp",EDGE,"E69")}),1.0]])]});
            extrude(context, id + "F109", {"entities" : qUnion([Q0]), "depth" : 200 * mm, "offsetDistance" : 25 * mm, "hasSecondDirection" : true, "secondDirectionOppositeDirection" : true, "secondDirectionDepth" : 200 * mm});
        }
        {
            var Q0;
            Q0=qCreatedBy(makeId("Front.planeOp"),FACE);
            cPlane(context, id + "F110", {"entities" : qUnion([Q0]), "cplaneType" : CPlaneType.OFFSET, "offset" : 10.5 * mm, "oppositeDirection" : true, "width" : 150 * mm, "height" : 150 * mm});
        }
        {
            var Q0;
            Q0=makeQuery(id+"F35.opExtrude","CAP_FACE",FACE,{"disambiguationData":[OSD([sQuery(id+"F34.wireOp",EDGE,"E43")])],"isStart":true});
            var sketch = newSketch(context, id + "F111", { "sketchPlane" : qUnion([Q0])});
            skCircle(sketch, "E71", {"center": v(1448.89, 150) * mm, "radius": 8.5 * mm});
            skSolve(sketch);
        }
        {
            var Q0;
            Q0 = qSketchRegion(id + "F111", true);
            extrude(context, id + "F112", {"entities" : qUnion([Q0]), "operationType" : NewBodyOperationType.REMOVE, "oppositeDirection" : true, "depth" : 600 * mm, "offsetDistance" : 25 * mm});
        }
        {
            var Q0;
            Q0=makeQuery(id+"F38.opExtrude","CAP_FACE",FACE,{"disambiguationData":[OSD([sQuery(id+"F37.wireOp",EDGE,"E44")])],"isStart":false});
            var sketch = newSketch(context, id + "F113", { "sketchPlane" : qUnion([Q0])});
            skCircle(sketch, "E72", {"center": v(1207.4, 150) * mm, "radius": 8.5 * mm});
            skSolve(sketch);
        }
        {
            var Q0;
            Q0 = qSketchRegion(id + "F113", true);
            extrude(context, id + "F114", {"entities" : qUnion([Q0]), "operationType" : NewBodyOperationType.REMOVE, "oppositeDirection" : true, "depth" : 600 * mm, "offsetDistance" : 25 * mm});
        }
        {
            var Q0;
            Q0=makeQuery(id+"F41.opExtrude","CAP_FACE",FACE,{"disambiguationData":[OSD([sQuery(id+"F40.wireOp",EDGE,"E45")])],"isStart":false});
            var sketch = newSketch(context, id + "F115", { "sketchPlane" : qUnion([Q0])});
            skCircle(sketch, "E73", {"center": v(965.93, 150) * mm, "radius": 8.5 * mm});
            skSolve(sketch);
        }
        {
            var Q0;
            Q0 = qSketchRegion(id + "F115", true);
            extrude(context, id + "F116", {"entities" : qUnion([Q0]), "operationType" : NewBodyOperationType.REMOVE, "oppositeDirection" : true, "depth" : 600 * mm, "offsetDistance" : 25 * mm});
        }
        {
            var Q0;
            Q0=makeQuery(id+"F44.opExtrude","CAP_FACE",FACE,{"disambiguationData":[OSD([sQuery(id+"F43.wireOp",EDGE,"E46")])],"isStart":false});
            var sketch = newSketch(context, id + "F117", { "sketchPlane" : qUnion([Q0])});
            skCircle(sketch, "E74", {"center": v(724.44, 150) * mm, "radius": 8.5 * mm});
            skSolve(sketch);
        }
        {
            var Q0;
            Q0 = qSketchRegion(id + "F117", true);
            extrude(context, id + "F118", {"entities" : qUnion([Q0]), "operationType" : NewBodyOperationType.REMOVE, "oppositeDirection" : true, "depth" : 600 * mm, "offsetDistance" : 25 * mm});
        }
        {
            var Q0;
            Q0=makeQuery(id+"F47.opExtrude","CAP_FACE",FACE,{"disambiguationData":[OSD([sQuery(id+"F46.wireOp",EDGE,"E47")])],"isStart":false});
            var sketch = newSketch(context, id + "F119", { "sketchPlane" : qUnion([Q0])});
            skCircle(sketch, "E75", {"center": v(482.96, 150) * mm, "radius": 8.5 * mm});
            skSolve(sketch);
        }
        {
            var Q0;
            Q0 = qSketchRegion(id + "F119", true);
            extrude(context, id + "F120", {"entities" : qUnion([Q0]), "operationType" : NewBodyOperationType.REMOVE, "oppositeDirection" : true, "depth" : 600 * mm, "offsetDistance" : 25 * mm});
        }
        {
            var Q0;
            Q0=makeQuery(id+"F50.opExtrude","CAP_FACE",FACE,{"disambiguationData":[OSD([sQuery(id+"F49.wireOp",EDGE,"E48")])],"isStart":false});
            var sketch = newSketch(context, id + "F121", { "sketchPlane" : qUnion([Q0])});
            skCircle(sketch, "E76", {"center": v(241.48, 150) * mm, "radius": 8.5 * mm});
            skSolve(sketch);
        }
        {
            var Q0;
            Q0 = qSketchRegion(id + "F121", true);
            extrude(context, id + "F122", {"entities" : qUnion([Q0]), "operationType" : NewBodyOperationType.REMOVE, "oppositeDirection" : true, "depth" : 600 * mm, "offsetDistance" : 25 * mm});
        }
        {
            var Q0;
            Q0=makeQuery(id+"F53.opExtrude","CAP_FACE",FACE,{"disambiguationData":[OSD([sQuery(id+"F52.wireOp",EDGE,"E49")])],"isStart":false});
            var sketch = newSketch(context, id + "F123", { "sketchPlane" : qUnion([Q0])});
            skCircle(sketch, "E77", {"center": v(1448.89, -150) * mm, "radius": 8.5 * mm});
            skSolve(sketch);
        }
        {
            var Q0;
            Q0 = qSketchRegion(id + "F123", true);
            extrude(context, id + "F124", {"entities" : qUnion([Q0]), "operationType" : NewBodyOperationType.REMOVE, "oppositeDirection" : true, "depth" : 300 * mm, "offsetDistance" : 25 * mm});
        }
        {
            var Q0;
            Q0=makeQuery(id+"F56.opExtrude","CAP_FACE",FACE,{"disambiguationData":[OSD([sQuery(id+"F55.wireOp",EDGE,"E50")])],"isStart":false});
            var sketch = newSketch(context, id + "F125", { "sketchPlane" : qUnion([Q0])});
            skCircle(sketch, "E78", {"center": v(1207.4, -150) * mm, "radius": 8.5 * mm});
            skSolve(sketch);
        }
        {
            var Q0;
            Q0 = qSketchRegion(id + "F125", true);
            extrude(context, id + "F126", {"entities" : qUnion([Q0]), "operationType" : NewBodyOperationType.REMOVE, "oppositeDirection" : true, "depth" : 300 * mm, "offsetDistance" : 25 * mm});
        }
        {
            var Q0;
            Q0=makeQuery(id+"F59.opExtrude","CAP_FACE",FACE,{"disambiguationData":[OSD([sQuery(id+"F58.wireOp",EDGE,"E51")])],"isStart":false});
            var sketch = newSketch(context, id + "F127", { "sketchPlane" : qUnion([Q0])});
            skCircle(sketch, "E79", {"center": v(965.93, -150) * mm, "radius": 8.5 * mm});
            skSolve(sketch);
        }
        {
            var Q0;
            Q0 = qSketchRegion(id + "F127", true);
            extrude(context, id + "F128", {"entities" : qUnion([Q0]), "operationType" : NewBodyOperationType.REMOVE, "oppositeDirection" : true, "depth" : 300 * mm, "offsetDistance" : 25 * mm});
        }
        {
            var Q0;
            Q0=makeQuery(id+"F62.opExtrude","CAP_FACE",FACE,{"disambiguationData":[OSD([sQuery(id+"F61.wireOp",EDGE,"E52")])],"isStart":false});
            var sketch = newSketch(context, id + "F129", { "sketchPlane" : qUnion([Q0])});
            skCircle(sketch, "E80", {"center": v(724.44, -150) * mm, "radius": 8.5 * mm});
            skSolve(sketch);
        }
        {
            var Q0;
            Q0 = qSketchRegion(id + "F129", true);
            extrude(context, id + "F130", {"entities" : qUnion([Q0]), "operationType" : NewBodyOperationType.REMOVE, "oppositeDirection" : true, "depth" : 300 * mm, "offsetDistance" : 25 * mm});
        }
        {
            var Q0;
            Q0=makeQuery(id+"F65.opExtrude","CAP_FACE",FACE,{"disambiguationData":[OSD([sQuery(id+"F64.wireOp",EDGE,"E53")])],"isStart":false});
            var sketch = newSketch(context, id + "F131", { "sketchPlane" : qUnion([Q0])});
            skCircle(sketch, "E81", {"center": v(482.96, -150) * mm, "radius": 8.5 * mm});
            skSolve(sketch);
        }
        {
            var Q0;
            Q0 = qSketchRegion(id + "F131", true);
            extrude(context, id + "F132", {"entities" : qUnion([Q0]), "operationType" : NewBodyOperationType.REMOVE, "oppositeDirection" : true, "depth" : 300 * mm, "offsetDistance" : 25 * mm});
        }
        {
            var Q0;
            Q0=makeQuery(id+"F68.opExtrude","CAP_FACE",FACE,{"disambiguationData":[OSD([sQuery(id+"F67.wireOp",EDGE,"E54")])],"isStart":false});
            var sketch = newSketch(context, id + "F133", { "sketchPlane" : qUnion([Q0])});
            skCircle(sketch, "E82", {"center": v(241.48, -150) * mm, "radius": 8.5 * mm});
            skSolve(sketch);
        }
        {
            var Q0;
            Q0 = qSketchRegion(id + "F133", true);
            extrude(context, id + "F134", {"entities" : qUnion([Q0]), "operationType" : NewBodyOperationType.REMOVE, "oppositeDirection" : true, "depth" : 300 * mm, "offsetDistance" : 25 * mm});
        }
        {
            var Q0;
            Q0=makeQuery(id+"F71.opExtrude","CAP_FACE",FACE,{"disambiguationData":[OSD([sQuery(id+"F70.wireOp",EDGE,"E55")])],"isStart":false});
            var sketch = newSketch(context, id + "F135", { "sketchPlane" : qUnion([Q0])});
            skCircle(sketch, "E83", {"center": v(-1448.89, -150) * mm, "radius": 8.5 * mm});
            skSolve(sketch);
        }
        {
            var Q0;
            Q0 = qSketchRegion(id + "F135", true);
            extrude(context, id + "F136", {"entities" : qUnion([Q0]), "operationType" : NewBodyOperationType.REMOVE, "oppositeDirection" : true, "depth" : 600 * mm, "offsetDistance" : 25 * mm});
        }
        {
            var Q0;
            Q0=makeQuery(id+"F74.opExtrude","CAP_FACE",FACE,{"disambiguationData":[OSD([sQuery(id+"F73.wireOp",EDGE,"E56")])],"isStart":false});
            var sketch = newSketch(context, id + "F137", { "sketchPlane" : qUnion([Q0])});
            skCircle(sketch, "E84", {"center": v(-1207.4, -150) * mm, "radius": 8.5 * mm});
            skSolve(sketch);
        }
        {
            var Q0;
            Q0 = qSketchRegion(id + "F137", true);
            extrude(context, id + "F138", {"entities" : qUnion([Q0]), "operationType" : NewBodyOperationType.REMOVE, "oppositeDirection" : true, "depth" : 600 * mm, "offsetDistance" : 25 * mm});
        }
        {
            var Q0;
            Q0=makeQuery(id+"F77.opExtrude","CAP_FACE",FACE,{"disambiguationData":[OSD([sQuery(id+"F76.wireOp",EDGE,"E57")])],"isStart":false});
            var sketch = newSketch(context, id + "F139", { "sketchPlane" : qUnion([Q0])});
            skCircle(sketch, "E85", {"center": v(-965.93, -150) * mm, "radius": 8.5 * mm});
            skSolve(sketch);
        }
        {
            var Q0;
            Q0 = qSketchRegion(id + "F139", true);
            extrude(context, id + "F140", {"entities" : qUnion([Q0]), "operationType" : NewBodyOperationType.REMOVE, "oppositeDirection" : true, "depth" : 600 * mm, "offsetDistance" : 25 * mm});
        }
        {
            var Q0;
            Q0=makeQuery(id+"F80.opExtrude","CAP_FACE",FACE,{"disambiguationData":[OSD([sQuery(id+"F79.wireOp",EDGE,"E58")])],"isStart":false});
            var sketch = newSketch(context, id + "F141", { "sketchPlane" : qUnion([Q0])});
            skCircle(sketch, "E86", {"center": v(-724.44, -150) * mm, "radius": 8.5 * mm});
            skSolve(sketch);
        }
        {
            var Q0;
            Q0 = qSketchRegion(id + "F141", true);
            extrude(context, id + "F142", {"entities" : qUnion([Q0]), "operationType" : NewBodyOperationType.REMOVE, "oppositeDirection" : true, "depth" : 600 * mm, "offsetDistance" : 25 * mm});
        }
        {
            var Q0;
            Q0=makeQuery(id+"F83.opExtrude","CAP_FACE",FACE,{"disambiguationData":[OSD([sQuery(id+"F82.wireOp",EDGE,"E59")])],"isStart":false});
            var sketch = newSketch(context, id + "F143", { "sketchPlane" : qUnion([Q0])});
            skCircle(sketch, "E87", {"center": v(-482.96, -150) * mm, "radius": 8.5 * mm});
            skSolve(sketch);
        }
        {
            var Q0;
            Q0 = qSketchRegion(id + "F143", true);
            extrude(context, id + "F144", {"entities" : qUnion([Q0]), "operationType" : NewBodyOperationType.REMOVE, "oppositeDirection" : true, "depth" : 600 * mm, "offsetDistance" : 25 * mm});
        }
        {
            var Q0;
            Q0=makeQuery(id+"F86.opExtrude","CAP_FACE",FACE,{"disambiguationData":[OSD([sQuery(id+"F85.wireOp",EDGE,"E60")])],"isStart":false});
            var sketch = newSketch(context, id + "F145", { "sketchPlane" : qUnion([Q0])});
            skCircle(sketch, "E88", {"center": v(-241.48, -150) * mm, "radius": 8.5 * mm});
            skSolve(sketch);
        }
        {
            var Q0;
            Q0 = qSketchRegion(id + "F145", true);
            extrude(context, id + "F146", {"entities" : qUnion([Q0]), "operationType" : NewBodyOperationType.REMOVE, "oppositeDirection" : true, "depth" : 600 * mm, "offsetDistance" : 25 * mm});
        }
        {
            var Q0;
            Q0=makeQuery(id+"F89.opExtrude","CAP_FACE",FACE,{"disambiguationData":[OSD([sQuery(id+"F88.wireOp",EDGE,"E61")])],"isStart":false});
            var sketch = newSketch(context, id + "F147", { "sketchPlane" : qUnion([Q0])});
            skCircle(sketch, "E89", {"center": v(-1448.89, 150) * mm, "radius": 8.5 * mm});
            skSolve(sketch);
        }
        {
            var Q0;
            Q0 = qSketchRegion(id + "F147", true);
            extrude(context, id + "F148", {"entities" : qUnion([Q0]), "operationType" : NewBodyOperationType.REMOVE, "oppositeDirection" : true, "depth" : 300 * mm, "offsetDistance" : 25 * mm});
        }
        {
            var Q0;
            Q0=makeQuery(id+"F92.opExtrude","CAP_FACE",FACE,{"disambiguationData":[OSD([sQuery(id+"F91.wireOp",EDGE,"E62")])],"isStart":false});
            var sketch = newSketch(context, id + "F149", { "sketchPlane" : qUnion([Q0])});
            skCircle(sketch, "E90", {"center": v(-1207.4, 150) * mm, "radius": 8.5 * mm});
            skSolve(sketch);
        }
        {
            var Q0;
            Q0 = qSketchRegion(id + "F149", true);
            extrude(context, id + "F150", {"entities" : qUnion([Q0]), "operationType" : NewBodyOperationType.REMOVE, "oppositeDirection" : true, "depth" : 300 * mm, "offsetDistance" : 25 * mm});
        }
        {
            var Q0;
            Q0=makeQuery(id+"F95.opExtrude","CAP_FACE",FACE,{"disambiguationData":[OSD([sQuery(id+"F94.wireOp",EDGE,"E63")])],"isStart":false});
            var sketch = newSketch(context, id + "F151", { "sketchPlane" : qUnion([Q0])});
            skCircle(sketch, "E91", {"center": v(-965.93, 150) * mm, "radius": 8.5 * mm});
            skSolve(sketch);
        }
        {
            var Q0;
            Q0 = qSketchRegion(id + "F151", true);
            extrude(context, id + "F152", {"entities" : qUnion([Q0]), "operationType" : NewBodyOperationType.REMOVE, "oppositeDirection" : true, "depth" : 300 * mm, "offsetDistance" : 25 * mm});
        }
        {
            var Q0;
            Q0=makeQuery(id+"F98.opExtrude","CAP_FACE",FACE,{"disambiguationData":[OSD([sQuery(id+"F97.wireOp",EDGE,"E64")])],"isStart":false});
            var sketch = newSketch(context, id + "F153", { "sketchPlane" : qUnion([Q0])});
            skCircle(sketch, "E92", {"center": v(-724.44, 150) * mm, "radius": 8.5 * mm});
            skSolve(sketch);
        }
        {
            var Q0;
            Q0 = qSketchRegion(id + "F153", true);
            extrude(context, id + "F154", {"entities" : qUnion([Q0]), "operationType" : NewBodyOperationType.REMOVE, "oppositeDirection" : true, "depth" : 300 * mm, "offsetDistance" : 25 * mm});
        }
        {
            var Q0;
            Q0=makeQuery(id+"F101.opExtrude","CAP_FACE",FACE,{"disambiguationData":[OSD([sQuery(id+"F100.wireOp",EDGE,"E65")])],"isStart":false});
            var sketch = newSketch(context, id + "F155", { "sketchPlane" : qUnion([Q0])});
            skCircle(sketch, "E93", {"center": v(-482.96, 150) * mm, "radius": 8.5 * mm});
            skSolve(sketch);
        }
        {
            var Q0;
            Q0 = qSketchRegion(id + "F155", true);
            extrude(context, id + "F156", {"entities" : qUnion([Q0]), "operationType" : NewBodyOperationType.REMOVE, "oppositeDirection" : true, "depth" : 300 * mm, "offsetDistance" : 25 * mm});
        }
        {
            var Q0;
            Q0=makeQuery(id+"F104.opExtrude","CAP_FACE",FACE,{"disambiguationData":[OSD([sQuery(id+"F103.wireOp",EDGE,"E66")])],"isStart":false});
            var sketch = newSketch(context, id + "F157", { "sketchPlane" : qUnion([Q0])});
            skCircle(sketch, "E94", {"center": v(-241.48, 150) * mm, "radius": 8.5 * mm});
            skSolve(sketch);
        }
        {
            var Q0;
            Q0 = qSketchRegion(id + "F157", true);
            extrude(context, id + "F158", {"entities" : qUnion([Q0]), "operationType" : NewBodyOperationType.REMOVE, "oppositeDirection" : true, "depth" : 300 * mm, "offsetDistance" : 25 * mm});
        }
        {
            var Q0;
            Q0=qCreatedBy(id+"F110.planeOp",FACE);
            var sketch = newSketch(context, id + "F159", { "sketchPlane" : qUnion([Q0])});
            skLineSegment(sketch, "E95.bottom", {"start": v(450, 199.5) * mm, "end": v(333, 199.5) * mm});
            skLineSegment(sketch, "E95.top", {"start": v(450, 114.5) * mm, "end": v(333, 114.5) * mm});
            skLineSegment(sketch, "E95.left", {"start": v(450, 199.5) * mm, "end": v(450, 114.5) * mm});
            skLineSegment(sketch, "E95.right", {"start": v(333, 199.5) * mm, "end": v(333, 114.5) * mm});
            skLineSegment(sketch, "E96", {"start": v(450, 182.05) * mm, "end": v(450, 182.05) * mm});
            skCircle(sketch, "E97", {"center": v(431.5, 187) * mm, "radius": 4.5 * mm});
            skCircle(sketch, "E98", {"center": v(351.5, 187) * mm, "radius": 4.5 * mm});
            skCircle(sketch, "E99", {"center": v(431.5, 127) * mm, "radius": 4.5 * mm});
            skCircle(sketch, "E100", {"center": v(351.5, 127) * mm, "radius": 4.5 * mm});
            skLineSegment(sketch, "E101.bottom", {"start": v(427, 187) * mm, "end": v(356, 187) * mm, "construction": true});
            skLineSegment(sketch, "E101.top", {"start": v(427, 127) * mm, "end": v(356, 127) * mm, "construction": true});
            skLineSegment(sketch, "E101.left", {"start": v(431.5, 182.5) * mm, "end": v(431.5, 131.5) * mm, "construction": true});
            skLineSegment(sketch, "E101.right", {"start": v(351.5, 182.5) * mm, "end": v(351.5, 131.5) * mm, "construction": true});
            skLineSegment(sketch, "E102", {"start": v(391.5, 187) * mm, "end": v(391.5, 127) * mm});
            skLineSegment(sketch, "E103", {"start": v(391.5, 199.5) * mm, "end": v(391.5, 114.5) * mm, "construction": true});
            skLineSegment(sketch, "E104", {"start": v(450, 157) * mm, "end": v(333, 157) * mm, "construction": true});
            skLineSegment(sketch, "E105", {"start": v(431.5, 157) * mm, "end": v(351.5, 157) * mm});
            skLineSegment(sketch, "E106", {"start": v(0, 0) * mm, "end": v(-163.18, 0) * mm, "construction": true});
            skLineSegment(sketch, "E107", {"start": v(0, 0) * mm, "end": v(0, -90.52) * mm, "construction": true});
            skLineSegment(sketch, "E108.MirrorCS", {"start": v(-450, 114.5) * mm, "end": v(-333, 114.5) * mm});
            skLineSegment(sketch, "E109.MirrorCS", {"start": v(-450, 199.5) * mm, "end": v(-450, 114.5) * mm});
            skLineSegment(sketch, "E110.MirrorCS", {"start": v(-333, 199.5) * mm, "end": v(-333, 114.5) * mm});
            skLineSegment(sketch, "E111.MirrorCS", {"start": v(-450, 199.5) * mm, "end": v(-333, 199.5) * mm});
            skLineSegment(sketch, "E112.MirrorCS", {"start": v(216, 199.5) * mm, "end": v(333, 199.5) * mm});
            skLineSegment(sketch, "E113.MirrorCS", {"start": v(-450, -114.5) * mm, "end": v(-333, -114.5) * mm});
            skLineSegment(sketch, "E114.MirrorCS", {"start": v(-450, -199.5) * mm, "end": v(-333, -199.5) * mm});
            skLineSegment(sketch, "E115.MirrorCS", {"start": v(-333, -199.5) * mm, "end": v(-333, -114.5) * mm});
            skLineSegment(sketch, "E116.MirrorCS", {"start": v(-450, -199.5) * mm, "end": v(-450, -114.5) * mm});
            skLineSegment(sketch, "E117.MirrorCS", {"start": v(450, -114.5) * mm, "end": v(333, -114.5) * mm});
            skLineSegment(sketch, "E118.MirrorCS", {"start": v(450, -199.5) * mm, "end": v(333, -199.5) * mm});
            skLineSegment(sketch, "E119.MirrorCS", {"start": v(333, -199.5) * mm, "end": v(333, -114.5) * mm});
            skLineSegment(sketch, "E120.MirrorCS", {"start": v(450, -199.5) * mm, "end": v(450, -114.5) * mm});
            skCircle(sketch, "E121.MirrorC", {"center": v(-351.5, 127) * mm, "radius": 4.5 * mm});
            skCircle(sketch, "E122.MirrorC", {"center": v(-351.5, 187) * mm, "radius": 4.5 * mm});
            skCircle(sketch, "E123.MirrorC", {"center": v(-431.5, 187) * mm, "radius": 4.5 * mm});
            skCircle(sketch, "E124.MirrorC", {"center": v(-431.5, 127) * mm, "radius": 4.5 * mm});
            skCircle(sketch, "E125.MirrorC", {"center": v(-351.5, -127) * mm, "radius": 4.5 * mm});
            skCircle(sketch, "E126.MirrorC", {"center": v(-351.5, -187) * mm, "radius": 4.5 * mm});
            skCircle(sketch, "E127.MirrorC", {"center": v(-431.5, -187) * mm, "radius": 4.5 * mm});
            skCircle(sketch, "E128.MirrorC", {"center": v(-431.5, -127) * mm, "radius": 4.5 * mm});
            skCircle(sketch, "E129.MirrorC", {"center": v(351.5, -127) * mm, "radius": 4.5 * mm});
            skCircle(sketch, "E130.MirrorC", {"center": v(351.5, -187) * mm, "radius": 4.5 * mm});
            skCircle(sketch, "E131.MirrorC", {"center": v(431.5, -187) * mm, "radius": 4.5 * mm});
            skCircle(sketch, "E132.MirrorC", {"center": v(431.5, -127) * mm, "radius": 4.5 * mm});
            skLineSegment(sketch, "E133", {"start": v(450, 199.5) * mm, "end": v(450, 215) * mm});
            skSolve(sketch);
        }
        {
            var Q0;
            Q0 = qSketchRegion(id + "F159", true);
            extrude(context, id + "F160", {"entities" : qUnion([Q0]), "oppositeDirection" : true, "depth" : 4 * mm, "offsetDistance" : 25 * mm});
        }
        {
            var Q0;
            Q0=makeQuery(id+"F7.opExtrude","CAP_FACE",FACE,{"disambiguationData":[OSD([sQuery(id+"F0.wireOp",EDGE,"E6")])],"isStart":false});
            var sketch = newSketch(context, id + "F161", { "sketchPlane" : qUnion([Q0])});
            skCircle(sketch, "E134", {"center": v(0, -150) * mm, "radius": 8.5 * mm});
            skSolve(sketch);
        }
        {
            var Q0;
            Q0 = qSketchRegion(id + "F161", true);
            extrude(context, id + "F162", {"entities" : qUnion([Q0]), "operationType" : NewBodyOperationType.REMOVE, "oppositeDirection" : true, "depth" : 1600 * mm, "offsetDistance" : 25 * mm});
        }
    });
